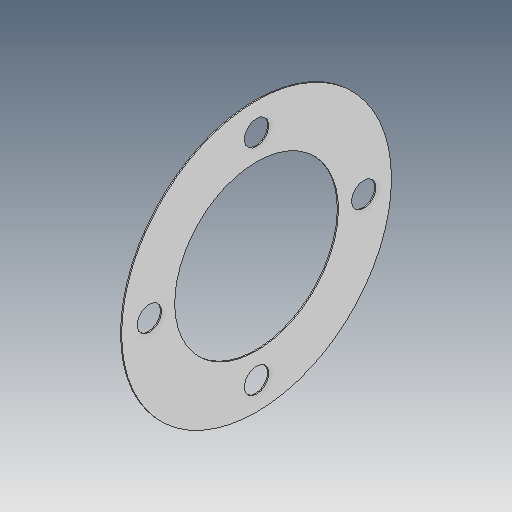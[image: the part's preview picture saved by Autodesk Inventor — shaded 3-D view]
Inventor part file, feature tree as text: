
AUTODESK INVENTOR PART (.ipt)
format: ipt  version: 2025 (Build 290162000, 162)  size: 303,616 bytes
history: native  units: in
note: dims shown in document units (in); Inventor stores cm internally (conversion verified against a paired STEP export)
features: sketch x2, extrude x1
ambient origin geometry x8: Origin, YZ Plane, XZ Plane, XY Plane, X Axis, Y Axis, Z Axis, Center Point
bodies: 实体1 (feature_tree)
feature tree (3):
  extrude  "拉伸1"  Depth=2.9134in
  sketch  "草图1"  dims[d0=0.4331in d2=2.9134in]
  sketch  "草图 - 环形阵列1"  dims[d1=4.8031in d3=2.9134in d4=0.4331in d5=1.9094in d6=1.5748in d8=360.0deg d10=0.0197in d11=0.0in]
